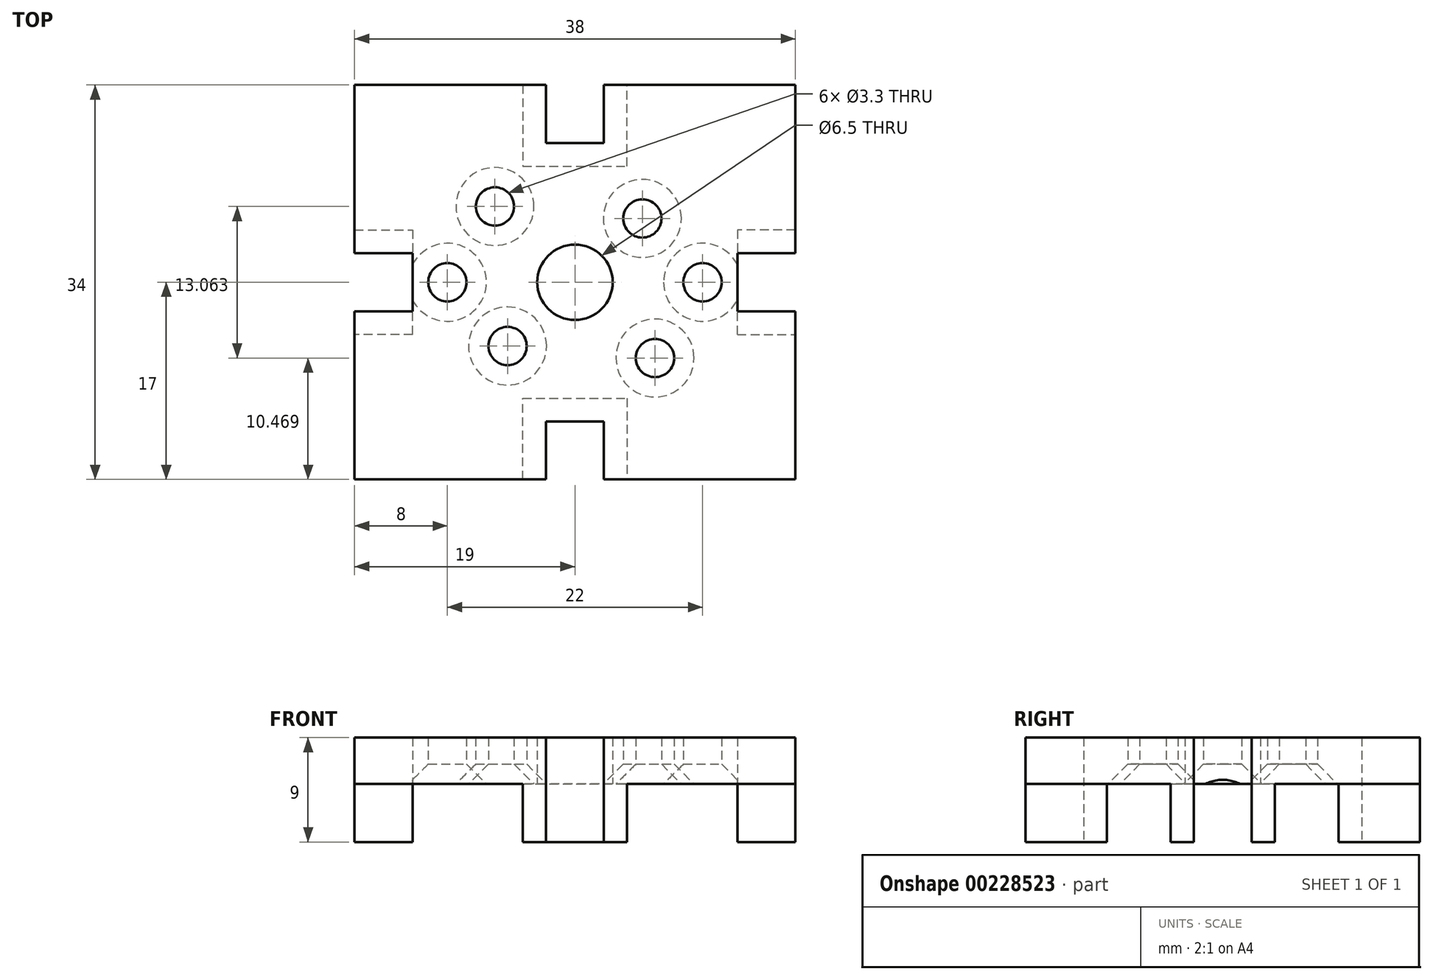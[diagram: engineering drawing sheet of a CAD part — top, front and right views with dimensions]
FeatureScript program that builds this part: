
annotation { "Feature Type Name" : "Feature", "Feature Type Description" : "" }
export const myFeature = defineFeature(function(context is Context, id is Id, definition is map)
    precondition{}
    {
        {
            var Q0;
            Q0=qCreatedBy(makeId("Top.planeOp"),FACE);
            var sketch = newSketch(context, id + "F0", { "sketchPlane" : qUnion([Q0])});
            skPoint(sketch, "E0.middle", {"position": v(0, 0) * mm});
            skLineSegment(sketch, "E1", {"start": v(-19, 17) * mm, "end": v(-2.5, 17) * mm});
            skLineSegment(sketch, "E2", {"start": v(-2.5, 17) * mm, "end": v(-2.5, 12) * mm});
            skLineSegment(sketch, "E3", {"start": v(-2.5, 12) * mm, "end": v(2.5, 12) * mm});
            skLineSegment(sketch, "E4", {"start": v(2.5, 12) * mm, "end": v(2.5, 17) * mm});
            skLineSegment(sketch, "E5", {"start": v(2.5, 17) * mm, "end": v(19, 17) * mm});
            skLineSegment(sketch, "E6.MirrorCS", {"start": v(-19, -17) * mm, "end": v(-2.5, -17) * mm});
            skLineSegment(sketch, "E7.MirrorCS", {"start": v(-2.5, -17) * mm, "end": v(-2.5, -12) * mm});
            skLineSegment(sketch, "E8.MirrorCS", {"start": v(-2.5, -12) * mm, "end": v(2.5, -12) * mm});
            skLineSegment(sketch, "E9.MirrorCS", {"start": v(2.5, -12) * mm, "end": v(2.5, -17) * mm});
            skLineSegment(sketch, "E10.MirrorCS", {"start": v(2.5, -17) * mm, "end": v(19, -17) * mm});
            skLineSegment(sketch, "E11", {"start": v(19, 17) * mm, "end": v(19, 2.5) * mm});
            skLineSegment(sketch, "E12", {"start": v(19, 2.5) * mm, "end": v(14, 2.5) * mm});
            skLineSegment(sketch, "E13", {"start": v(14, 2.5) * mm, "end": v(14, -2.5) * mm});
            skLineSegment(sketch, "E14", {"start": v(14, -2.5) * mm, "end": v(19, -2.5) * mm});
            skLineSegment(sketch, "E15", {"start": v(19, -2.5) * mm, "end": v(19, -17) * mm});
            skLineSegment(sketch, "E16.MirrorCS", {"start": v(-19, 17) * mm, "end": v(-19, 2.5) * mm});
            skLineSegment(sketch, "E17.MirrorCS", {"start": v(-19, 2.5) * mm, "end": v(-14, 2.5) * mm});
            skLineSegment(sketch, "E18.MirrorCS", {"start": v(-14, 2.5) * mm, "end": v(-14, -2.5) * mm});
            skLineSegment(sketch, "E19.MirrorCS", {"start": v(-14, -2.5) * mm, "end": v(-19, -2.5) * mm});
            skLineSegment(sketch, "E20.MirrorCS", {"start": v(-19, -2.5) * mm, "end": v(-19, -17) * mm});
            skCircle(sketch, "E21", {"center": v(0, 0) * mm, "radius": 3.25 * mm});
            skCircle(sketch, "E22", {"center": v(-11, 0) * mm, "radius": 1.6 * mm});
            skCircle(sketch, "E23.MirrorC", {"center": v(11, 0) * mm, "radius": 1.6 * mm});
            skCircle(sketch, "E24", {"center": v(-6.9, 6.53) * mm, "radius": 1.6 * mm});
            skCircle(sketch, "E25.MirrorC", {"center": v(6.9, -6.53) * mm, "radius": 1.6 * mm});
            skCircle(sketch, "E26.MirrorC", {"center": v(-5.8, -5.5) * mm, "radius": 1.6 * mm});
            skCircle(sketch, "E27.MirrorC", {"center": v(5.8, 5.5) * mm, "radius": 1.6 * mm});
            skSolve(sketch);
        }
        {
            var Q0;
            Q0 = qSketchRegion(id + "F0", true);
            var Q1;
            Q1=sQuery(id+"F0.wireOp",EDGE,"sE7ihf6R-RHx5-mMTk-rBD1-R0r8pSJKT0Rv.top");
            extrude(context, id + "F1", {"entities" : qUnion([Q0]), "surfaceEntities" : qUnion([Q1]), "depth" : 4 * mm, "offsetDistance" : 25 * mm});
        }
        {
            var Q0;
            Q0=sQuery(id+"F0.wireOp",VERTEX,"E22.center");
            var Q1;
            Q1=sQuery(id+"F0.wireOp",VERTEX,"E24.center");
            var Q2;
            Q2=sQuery(id+"F0.wireOp",VERTEX,"E27.MirrorC.center");
            var Q3;
            Q3=sQuery(id+"F0.wireOp",VERTEX,"E23.MirrorC.center");
            var Q4;
            Q4=sQuery(id+"F0.wireOp",VERTEX,"E25.MirrorC.center");
            var Q5;
            Q5=sQuery(id+"F0.wireOp",VERTEX,"E26.MirrorC.center");
            var Q6;
            Q6=makeQuery(id+"F1.opExtrude","SWEPT_BODY",BODY,{"disambiguationData":[OSD([sQuery(id+"F0.wireOp",EDGE,"E1"),sQuery(id+"F0.wireOp",EDGE,"E2"),sQuery(id+"F0.wireOp",EDGE,"E3"),sQuery(id+"F0.wireOp",EDGE,"E4"),sQuery(id+"F0.wireOp",EDGE,"E5"),sQuery(id+"F0.wireOp",EDGE,"E6.MirrorCS"),sQuery(id+"F0.wireOp",EDGE,"E7.MirrorCS"),sQuery(id+"F0.wireOp",EDGE,"E8.MirrorCS"),sQuery(id+"F0.wireOp",EDGE,"E9.MirrorCS"),sQuery(id+"F0.wireOp",EDGE,"E10.MirrorCS"),sQuery(id+"F0.wireOp",EDGE,"E11"),sQuery(id+"F0.wireOp",EDGE,"E12"),sQuery(id+"F0.wireOp",EDGE,"E13"),sQuery(id+"F0.wireOp",EDGE,"E14"),sQuery(id+"F0.wireOp",EDGE,"E15"),sQuery(id+"F0.wireOp",EDGE,"E16.MirrorCS"),sQuery(id+"F0.wireOp",EDGE,"E17.MirrorCS"),sQuery(id+"F0.wireOp",EDGE,"E18.MirrorCS"),sQuery(id+"F0.wireOp",EDGE,"E19.MirrorCS"),sQuery(id+"F0.wireOp",EDGE,"E20.MirrorCS"),sQuery(id+"F0.wireOp",EDGE,"E21"),sQuery(id+"F0.wireOp",EDGE,"E22"),sQuery(id+"F0.wireOp",EDGE,"E23.MirrorC"),sQuery(id+"F0.wireOp",EDGE,"E24"),sQuery(id+"F0.wireOp",EDGE,"E25.MirrorC"),sQuery(id+"F0.wireOp",EDGE,"E26.MirrorC"),sQuery(id+"F0.wireOp",EDGE,"E27.MirrorC")])]});
            hole(context, id + "F2", {"style" : HoleStyle.C_SINK, "endStyle" : HoleEndStyle.THROUGH, "oppositeDirection" : true, "standardTappedOrClearance" : lookupTablePath({ "standard" : "ISO", "fit" : "Normal", "size" : "M3", "type" : "Clearance" }), "standardBlindInLast" : lookupTablePath({ "fit" : "Standard", "standard" : "ISO", "size" : "M3", "type" : "Clearance" }), "holeDiameter" : 3.3 * mm, "cSinkDiameter" : 6.72 * mm, "cSinkAngle" : 90 * degree, "majorDiameter" : 5 * mm, "isTappedThrough" : true, "tappedDepth" : 12 * mm, "tapClearance" : 3, "locations" : qUnion([Q0, Q1, Q2, Q3, Q4, Q5]), "scope" : qUnion([Q6])});
        }
        {
            var Q0;
            Q0=sQuery(id+"F0.wireOp",EDGE,"E19.MirrorCS");
            var Q1;
            Q1=sQuery(id+"F0.wireOp",EDGE,"E17.MirrorCS");
            var Q2;
            Q2=sQuery(id+"F0.wireOp",EDGE,"E4");
            var Q3;
            Q3=sQuery(id+"F0.wireOp",EDGE,"E2");
            var Q4;
            Q4=sQuery(id+"F0.wireOp",EDGE,"E3");
            var Q5;
            Q5=sQuery(id+"F0.wireOp",EDGE,"E14");
            var Q6;
            Q6=sQuery(id+"F0.wireOp",EDGE,"E12");
            var Q7;
            Q7=sQuery(id+"F0.wireOp",EDGE,"E9.MirrorCS");
            var Q8;
            Q8=sQuery(id+"F0.wireOp",EDGE,"E8.MirrorCS");
            var Q9;
            Q9=sQuery(id+"F0.wireOp",EDGE,"E7.MirrorCS");
            extrude(context, id + "F3", {"bodyType" : ToolBodyType.SURFACE, "surfaceEntities" : qUnion([Q0, Q1, Q2, Q3, Q4, Q5, Q6, Q7, Q8, Q9]), "oppositeDirection" : true, "depth" : 5 * mm, "offsetDistance" : 25 * mm});
        }
        {
            var Q0;
            Q0=makeQuery(id+"F3.opExtrude","SWEPT_FACE",FACE,{"disambiguationData":[OSD([sQuery(id+"F0.wireOp",EDGE,"E7.MirrorCS")])]});
            var Q1;
            Q1=makeQuery(id+"F3.opExtrude","SWEPT_FACE",FACE,{"disambiguationData":[OSD([sQuery(id+"F0.wireOp",EDGE,"E2")])]});
            extrude(context, id + "F4", {"entities" : qUnion([Q0, Q1]), "operationType" : NewBodyOperationType.ADD, "depth" : 2 * mm, "offsetDistance" : 25 * mm});
        }
        {
            var Q0;
            Q0=makeQuery(id+"F4.opExtrude","SWEPT_FACE",FACE,{"disambiguationData":[OSD([sQuery(id+"F0.wireOp",VERTEX,"E7.MirrorCS.end")])]});
            var Q1;
            Q1=makeQuery(id+"F3.opExtrude","SWEPT_FACE",FACE,{"disambiguationData":[OSD([sQuery(id+"F0.wireOp",EDGE,"E8.MirrorCS")])]});
            var Q2;
            Q2=makeQuery(id+"F3.opExtrude","SWEPT_FACE",FACE,{"disambiguationData":[OSD([sQuery(id+"F0.wireOp",EDGE,"E17.MirrorCS")])]});
            var Q3;
            Q3=makeQuery(id+"F3.opExtrude","SWEPT_FACE",FACE,{"disambiguationData":[OSD([sQuery(id+"F0.wireOp",EDGE,"E12")])]});
            extrude(context, id + "F5", {"entities" : qUnion([Q0, Q1, Q2, Q3]), "operationType" : NewBodyOperationType.ADD, "depth" : 2 * mm, "offsetDistance" : 25 * mm});
        }
        {
            var Q0;
            Q0=makeQuery(id+"F3.opExtrude","SWEPT_FACE",FACE,{"disambiguationData":[OSD([sQuery(id+"F0.wireOp",EDGE,"E19.MirrorCS")])]});
            var Q1;
            Q1=makeQuery(id+"F3.opExtrude","SWEPT_FACE",FACE,{"disambiguationData":[OSD([sQuery(id+"F0.wireOp",EDGE,"E14")])]});
            var Q2;
            Q2=makeQuery(id+"F3.opExtrude","SWEPT_FACE",FACE,{"disambiguationData":[OSD([sQuery(id+"F0.wireOp",EDGE,"E3")])]});
            var Q3;
            Q3=makeQuery(id+"F4.opExtrude","SWEPT_FACE",FACE,{"disambiguationData":[OSD([sQuery(id+"F0.wireOp",VERTEX,"E3.start")])]});
            extrude(context, id + "F6", {"entities" : qUnion([Q0, Q1, Q2, Q3]), "operationType" : NewBodyOperationType.ADD, "depth" : 2 * mm, "offsetDistance" : 25 * mm});
        }
        {
            var Q0;
            Q0=makeQuery(id+"F3.opExtrude","SWEPT_FACE",FACE,{"disambiguationData":[OSD([sQuery(id+"F0.wireOp",EDGE,"E9.MirrorCS")])]});
            var Q1;
            Q1=makeQuery(id+"F5.opExtrude","SWEPT_FACE",FACE,{"disambiguationData":[OSD([sQuery(id+"F0.wireOp",VERTEX,"E8.MirrorCS.end")])]});
            var Q2;
            Q2=makeQuery(id+"F6.opExtrude","SWEPT_FACE",FACE,{"disambiguationData":[OSD([sQuery(id+"F0.wireOp",VERTEX,"E3.end")])]});
            var Q3;
            Q3=makeQuery(id+"F3.opExtrude","SWEPT_FACE",FACE,{"disambiguationData":[OSD([sQuery(id+"F0.wireOp",EDGE,"E4")])]});
            extrude(context, id + "F7", {"entities" : qUnion([Q0, Q1, Q2, Q3]), "operationType" : NewBodyOperationType.ADD, "depth" : 2 * mm, "offsetDistance" : 25 * mm});
        }
    });
